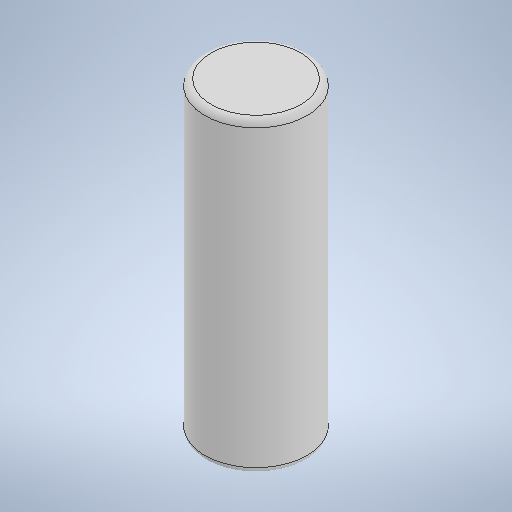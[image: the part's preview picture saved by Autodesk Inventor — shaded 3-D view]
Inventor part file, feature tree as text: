
AUTODESK INVENTOR PART (.ipt)
format: ipt  version: 2025.1 (Build 291241000, 241)  size: 265,728 bytes
history: native  units: mm
features: extrude x1, fillet x1, sketch x1
ambient origin geometry x8: Origin, YZ Plane, XZ Plane, XY Plane, X Axis, Y Axis, Z Axis, Center Point
bodies: Solid1 (feature_tree)
feature tree (3):
  extrude  "Extrusion1"  Depth=12.0mm TaperAngle=0.0deg
  fillet  "Fillet1"  Radius=0.25mm
  sketch  "Sketch1"  dims[d0=4.0mm d1=12.0mm d2=0.0mm d3=0.25mm]
